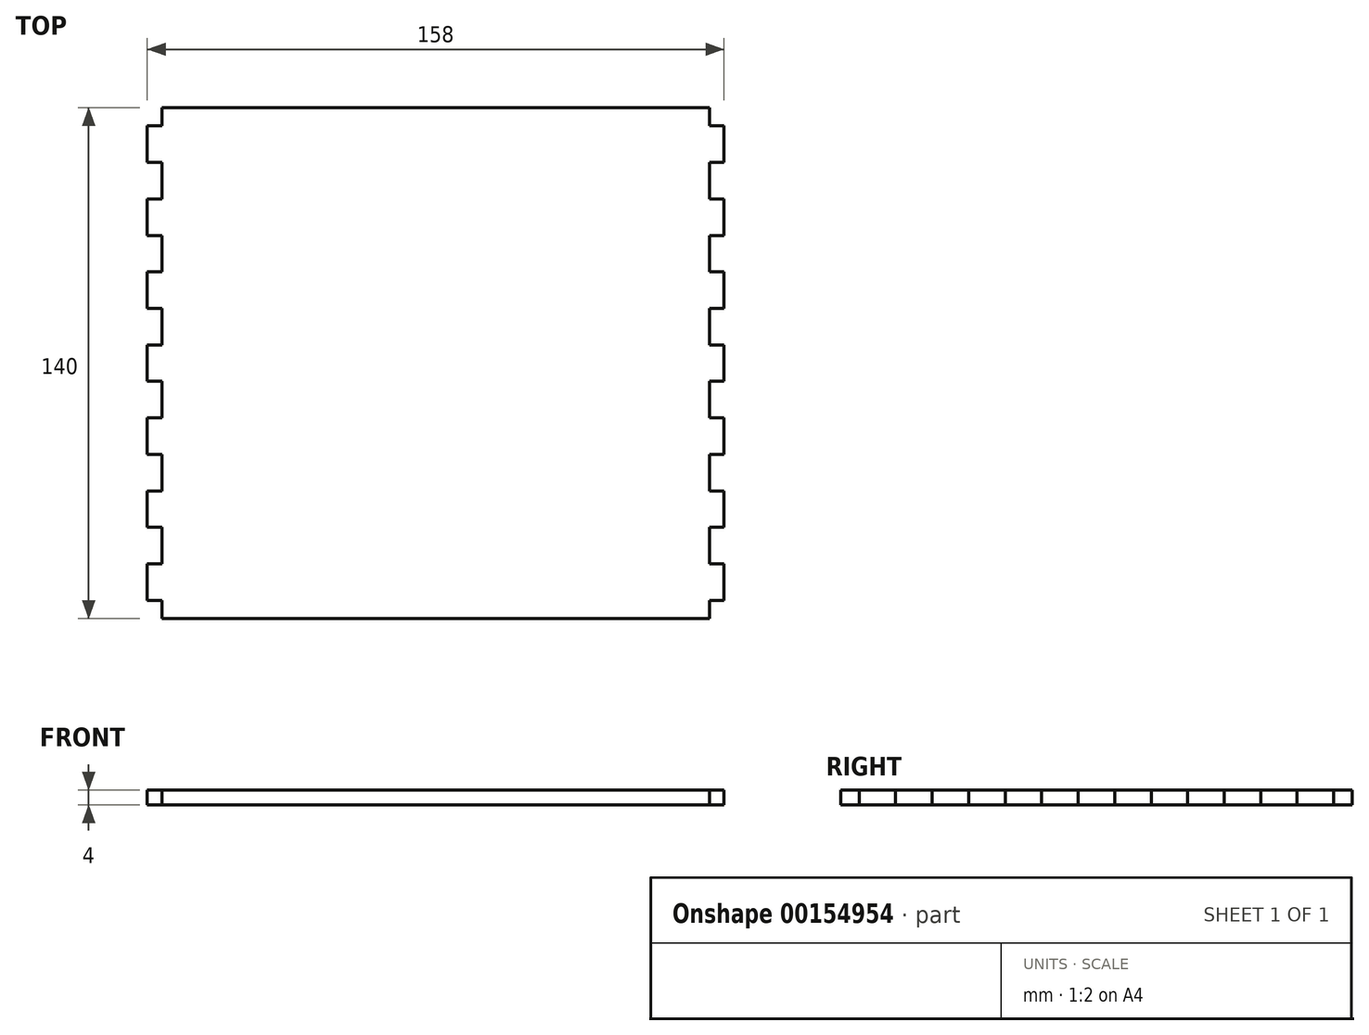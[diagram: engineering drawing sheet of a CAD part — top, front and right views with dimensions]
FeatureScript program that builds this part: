
annotation { "Feature Type Name" : "Feature", "Feature Type Description" : "" }
export const myFeature = defineFeature(function(context is Context, id is Id, definition is map)
    precondition{}
    {
        {
            var Q0;
            Q0=qCreatedBy(makeId("Top.planeOp"),FACE);
            var sketch = newSketch(context, id + "F0", { "sketchPlane" : qUnion([Q0])});
            skLineSegment(sketch, "E0.bottom", {"start": v(75, 70) * mm, "end": v(-75, 70) * mm});
            skLineSegment(sketch, "E0.top", {"start": v(75, -70) * mm, "end": v(-75, -70) * mm});
            skLineSegment(sketch, "E0.left", {"start": v(75, 70) * mm, "end": v(75, -70) * mm});
            skLineSegment(sketch, "E0.right", {"start": v(-75, 70) * mm, "end": v(-75, -70) * mm});
            skPoint(sketch, "E0.middle", {"position": v(0, 0) * mm});
            skSolve(sketch);
        }
        {
            var Q0;
            Q0 = qSketchRegion(id + "F0", true);
            extrude(context, id + "F1", {"entities" : qUnion([Q0]), "depth" : 4 * mm});
        }
        {
            var Q0;
            Q0=makeQuery(id+"F1.opExtrude","CAP_FACE",FACE,{"disambiguationData":[OSD([sQuery(id+"F0.wireOp",EDGE,"E0.bottom"),sQuery(id+"F0.wireOp",EDGE,"E0.top"),sQuery(id+"F0.wireOp",EDGE,"E0.left"),sQuery(id+"F0.wireOp",EDGE,"E0.right")])],"isStart":false});
            var sketch = newSketch(context, id + "F2", { "sketchPlane" : qUnion([Q0])});
            skLineSegment(sketch, "E1", {"start": v(-75, -70) * mm, "end": v(-75, -65) * mm});
            skLineSegment(sketch, "E2.bottom", {"start": v(-75, -65) * mm, "end": v(-79, -65) * mm});
            skLineSegment(sketch, "E2.top", {"start": v(-75, -55) * mm, "end": v(-79, -55) * mm});
            skLineSegment(sketch, "E2.left", {"start": v(-75, -65) * mm, "end": v(-75, -55) * mm});
            skLineSegment(sketch, "E2.right", {"start": v(-79, -65) * mm, "end": v(-79, -55) * mm});
            skLineSegment(sketch, "E3", {"start": v(0, 70) * mm, "end": v(0, 58.31) * mm});
            skPoint(sketch, "E3.endSnap0", {"position": v(0, 70) * mm});
            skLineSegment(sketch, "E4.0.1.0", {"start": v(-79, -45) * mm, "end": v(-79, -35) * mm});
            skLineSegment(sketch, "E4.0.1.1", {"start": v(-75, -45) * mm, "end": v(-75, -35) * mm});
            skLineSegment(sketch, "E4.0.1.2", {"start": v(-75, -50) * mm, "end": v(-75, -45) * mm});
            skLineSegment(sketch, "E4.0.1.3", {"start": v(-75, -35) * mm, "end": v(-79, -35) * mm});
            skLineSegment(sketch, "E4.0.1.4", {"start": v(-75, -45) * mm, "end": v(-79, -45) * mm});
            skLineSegment(sketch, "E4.0.2.0", {"start": v(-79, -25) * mm, "end": v(-79, -15) * mm});
            skLineSegment(sketch, "E4.0.2.1", {"start": v(-75, -25) * mm, "end": v(-75, -15) * mm});
            skLineSegment(sketch, "E4.0.2.2", {"start": v(-75, -30) * mm, "end": v(-75, -25) * mm});
            skLineSegment(sketch, "E4.0.2.3", {"start": v(-75, -15) * mm, "end": v(-79, -15) * mm});
            skLineSegment(sketch, "E4.0.2.4", {"start": v(-75, -25) * mm, "end": v(-79, -25) * mm});
            skLineSegment(sketch, "E4.0.3.0", {"start": v(-79, -5) * mm, "end": v(-79, 5) * mm});
            skLineSegment(sketch, "E4.0.3.1", {"start": v(-75, -5) * mm, "end": v(-75, 5) * mm});
            skLineSegment(sketch, "E4.0.3.2", {"start": v(-75, -10) * mm, "end": v(-75, -5) * mm});
            skLineSegment(sketch, "E4.0.3.3", {"start": v(-75, 5) * mm, "end": v(-79, 5) * mm});
            skLineSegment(sketch, "E4.0.3.4", {"start": v(-75, -5) * mm, "end": v(-79, -5) * mm});
            skLineSegment(sketch, "E4.0.4.0", {"start": v(-79, 15) * mm, "end": v(-79, 25) * mm});
            skLineSegment(sketch, "E4.0.4.1", {"start": v(-75, 15) * mm, "end": v(-75, 25) * mm});
            skLineSegment(sketch, "E4.0.4.2", {"start": v(-75, 10) * mm, "end": v(-75, 15) * mm});
            skLineSegment(sketch, "E4.0.4.3", {"start": v(-75, 25) * mm, "end": v(-79, 25) * mm});
            skLineSegment(sketch, "E4.0.4.4", {"start": v(-75, 15) * mm, "end": v(-79, 15) * mm});
            skLineSegment(sketch, "E4.0.5.0", {"start": v(-79, 35) * mm, "end": v(-79, 45) * mm});
            skLineSegment(sketch, "E4.0.5.1", {"start": v(-75, 35) * mm, "end": v(-75, 45) * mm});
            skLineSegment(sketch, "E4.0.5.2", {"start": v(-75, 30) * mm, "end": v(-75, 35) * mm});
            skLineSegment(sketch, "E4.0.5.3", {"start": v(-75, 45) * mm, "end": v(-79, 45) * mm});
            skLineSegment(sketch, "E4.0.5.4", {"start": v(-75, 35) * mm, "end": v(-79, 35) * mm});
            skLineSegment(sketch, "E4.0.6.0", {"start": v(-79, 55) * mm, "end": v(-79, 65) * mm});
            skLineSegment(sketch, "E4.0.6.1", {"start": v(-75, 55) * mm, "end": v(-75, 65) * mm});
            skLineSegment(sketch, "E4.0.6.2", {"start": v(-75, 50) * mm, "end": v(-75, 55) * mm});
            skLineSegment(sketch, "E4.0.6.3", {"start": v(-75, 65) * mm, "end": v(-79, 65) * mm});
            skLineSegment(sketch, "E4.0.6.4", {"start": v(-75, 55) * mm, "end": v(-79, 55) * mm});
            skLineSegment(sketch, "E4.direction1", {"start": v(-75, -70) * mm, "end": v(-50, -70) * mm, "construction": true});
            skLineSegment(sketch, "E4.direction2", {"start": v(-75, -70) * mm, "end": v(-75, -50) * mm, "construction": true});
            skLineSegment(sketch, "E5.MirrorCS", {"start": v(75, 5) * mm, "end": v(79, 5) * mm});
            skLineSegment(sketch, "E6.MirrorCS", {"start": v(75, 55) * mm, "end": v(79, 55) * mm});
            skLineSegment(sketch, "E7.MirrorCS", {"start": v(75, 65) * mm, "end": v(79, 65) * mm});
            skLineSegment(sketch, "E8.MirrorCS", {"start": v(75, 15) * mm, "end": v(79, 15) * mm});
            skLineSegment(sketch, "E9.MirrorCS", {"start": v(75, -45) * mm, "end": v(79, -45) * mm});
            skLineSegment(sketch, "E10.MirrorCS", {"start": v(75, -35) * mm, "end": v(79, -35) * mm});
            skLineSegment(sketch, "E11.MirrorCS", {"start": v(75, -50) * mm, "end": v(75, -45) * mm});
            skLineSegment(sketch, "E12.MirrorCS", {"start": v(75, -55) * mm, "end": v(79, -55) * mm});
            skLineSegment(sketch, "E13.MirrorCS", {"start": v(75, -65) * mm, "end": v(79, -65) * mm});
            skLineSegment(sketch, "E14.MirrorCS", {"start": v(75, -25) * mm, "end": v(79, -25) * mm});
            skLineSegment(sketch, "E15.MirrorCS", {"start": v(75, -15) * mm, "end": v(79, -15) * mm});
            skLineSegment(sketch, "E16.MirrorCS", {"start": v(75, 35) * mm, "end": v(79, 35) * mm});
            skLineSegment(sketch, "E17.MirrorCS", {"start": v(75, 25) * mm, "end": v(79, 25) * mm});
            skLineSegment(sketch, "E18.MirrorCS", {"start": v(75, -5) * mm, "end": v(79, -5) * mm});
            skLineSegment(sketch, "E19.MirrorCS", {"start": v(75, 45) * mm, "end": v(79, 45) * mm});
            skLineSegment(sketch, "E20.MirrorCS", {"start": v(75, -10) * mm, "end": v(75, -5) * mm});
            skLineSegment(sketch, "E21.MirrorCS", {"start": v(75, -30) * mm, "end": v(75, -25) * mm});
            skLineSegment(sketch, "E22.MirrorCS", {"start": v(75, 50) * mm, "end": v(75, 55) * mm});
            skLineSegment(sketch, "E23.MirrorCS", {"start": v(75, 30) * mm, "end": v(75, 35) * mm});
            skLineSegment(sketch, "E24.MirrorCS", {"start": v(75, 10) * mm, "end": v(75, 15) * mm});
            skLineSegment(sketch, "E25.MirrorCS", {"start": v(79, 35) * mm, "end": v(79, 45) * mm});
            skLineSegment(sketch, "E26.MirrorCS", {"start": v(75, 15) * mm, "end": v(75, 25) * mm});
            skLineSegment(sketch, "E27.MirrorCS", {"start": v(79, 55) * mm, "end": v(79, 65) * mm});
            skLineSegment(sketch, "E28.MirrorCS", {"start": v(75, -25) * mm, "end": v(75, -15) * mm});
            skLineSegment(sketch, "E29.MirrorCS", {"start": v(79, -25) * mm, "end": v(79, -15) * mm});
            skLineSegment(sketch, "E30.MirrorCS", {"start": v(75, -45) * mm, "end": v(75, -35) * mm});
            skLineSegment(sketch, "E31.MirrorCS", {"start": v(79, -45) * mm, "end": v(79, -35) * mm});
            skLineSegment(sketch, "E32.MirrorCS", {"start": v(79, -65) * mm, "end": v(79, -55) * mm});
            skLineSegment(sketch, "E33.MirrorCS", {"start": v(75, -65) * mm, "end": v(75, -55) * mm});
            skLineSegment(sketch, "E34.MirrorCS", {"start": v(75, -5) * mm, "end": v(75, 5) * mm});
            skLineSegment(sketch, "E35.MirrorCS", {"start": v(79, 15) * mm, "end": v(79, 25) * mm});
            skLineSegment(sketch, "E36.MirrorCS", {"start": v(75, 35) * mm, "end": v(75, 45) * mm});
            skLineSegment(sketch, "E37.MirrorCS", {"start": v(75, 55) * mm, "end": v(75, 65) * mm});
            skLineSegment(sketch, "E38.MirrorCS", {"start": v(79, -5) * mm, "end": v(79, 5) * mm});
            skLineSegment(sketch, "E39.MirrorCS", {"start": v(75, -70) * mm, "end": v(75, -65) * mm});
            skLineSegment(sketch, "E40.MirrorCS", {"start": v(75, -70) * mm, "end": v(75, -50) * mm, "construction": true});
            skSolve(sketch);
        }
        {
            var Q0;
            Q0 = qSketchRegion(id + "F2", true);
            extrude(context, id + "F3", {"entities" : qUnion([Q0]), "operationType" : NewBodyOperationType.ADD, "oppositeDirection" : true, "depth" : 4 * mm});
        }
    });
